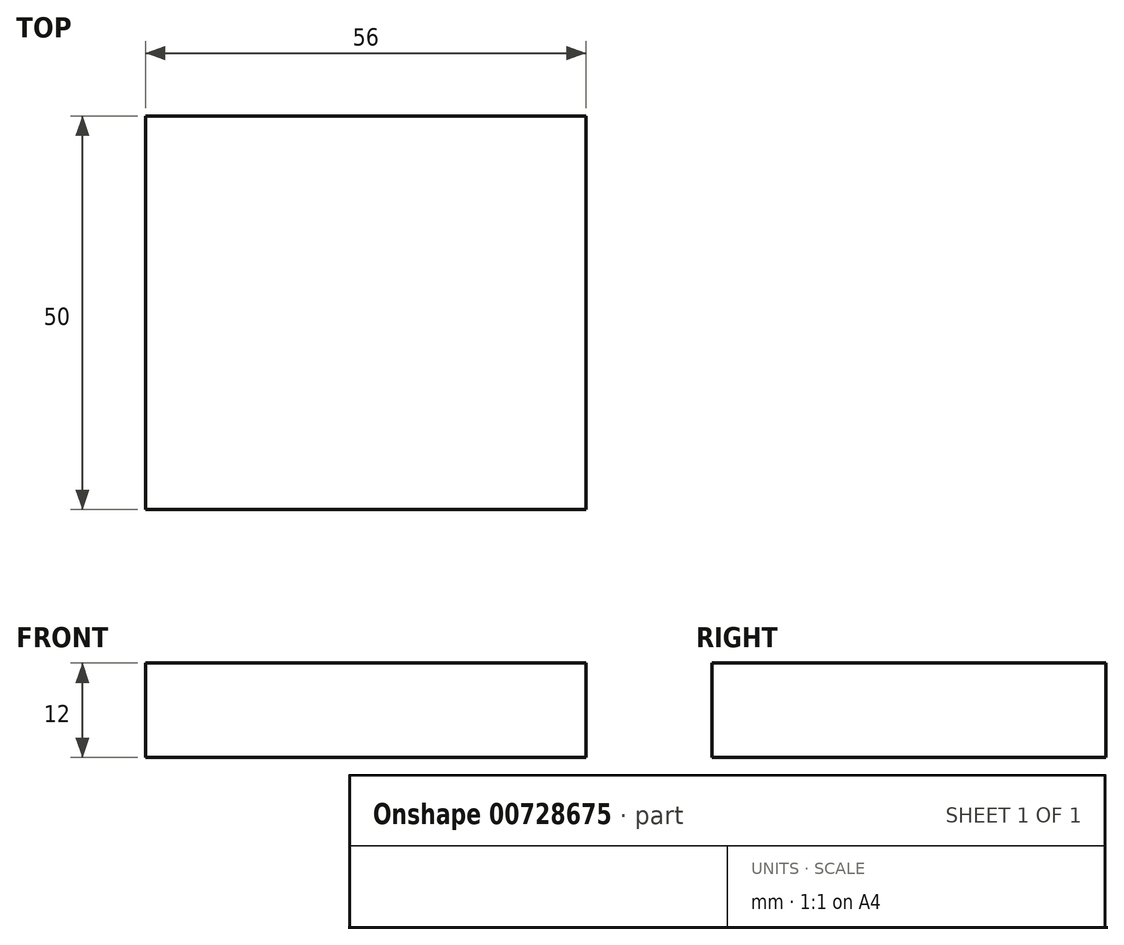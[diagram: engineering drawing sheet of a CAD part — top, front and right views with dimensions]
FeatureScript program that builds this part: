
annotation { "Feature Type Name" : "Feature", "Feature Type Description" : "" }
export const myFeature = defineFeature(function(context is Context, id is Id, definition is map)
    precondition{}
    {
        {
            var Q0;
            Q0=qCreatedBy(makeId("Top.planeOp"),FACE);
            var sketch = newSketch(context, id + "F0", { "sketchPlane" : qUnion([Q0])});
            skLineSegment(sketch, "E0.bottom", {"start": v(29.33, 25) * mm, "end": v(-26.67, 25) * mm});
            skLineSegment(sketch, "E0.top", {"start": v(29.33, -25) * mm, "end": v(-26.67, -25) * mm});
            skLineSegment(sketch, "E0.left", {"start": v(29.33, 25) * mm, "end": v(29.33, -25) * mm});
            skLineSegment(sketch, "E0.right", {"start": v(-26.67, 25) * mm, "end": v(-26.67, -25) * mm});
            skPoint(sketch, "E0.middle", {"position": v(1.33, 0) * mm});
            skSolve(sketch);
        }
        {
            var Q0;
            Q0 = qSketchRegion(id + "F0", true);
            extrude(context, id + "F1", {"entities" : qUnion([Q0]), "depth" : 12 * mm, "offsetDistance" : 25.4 * mm});
        }
    });
